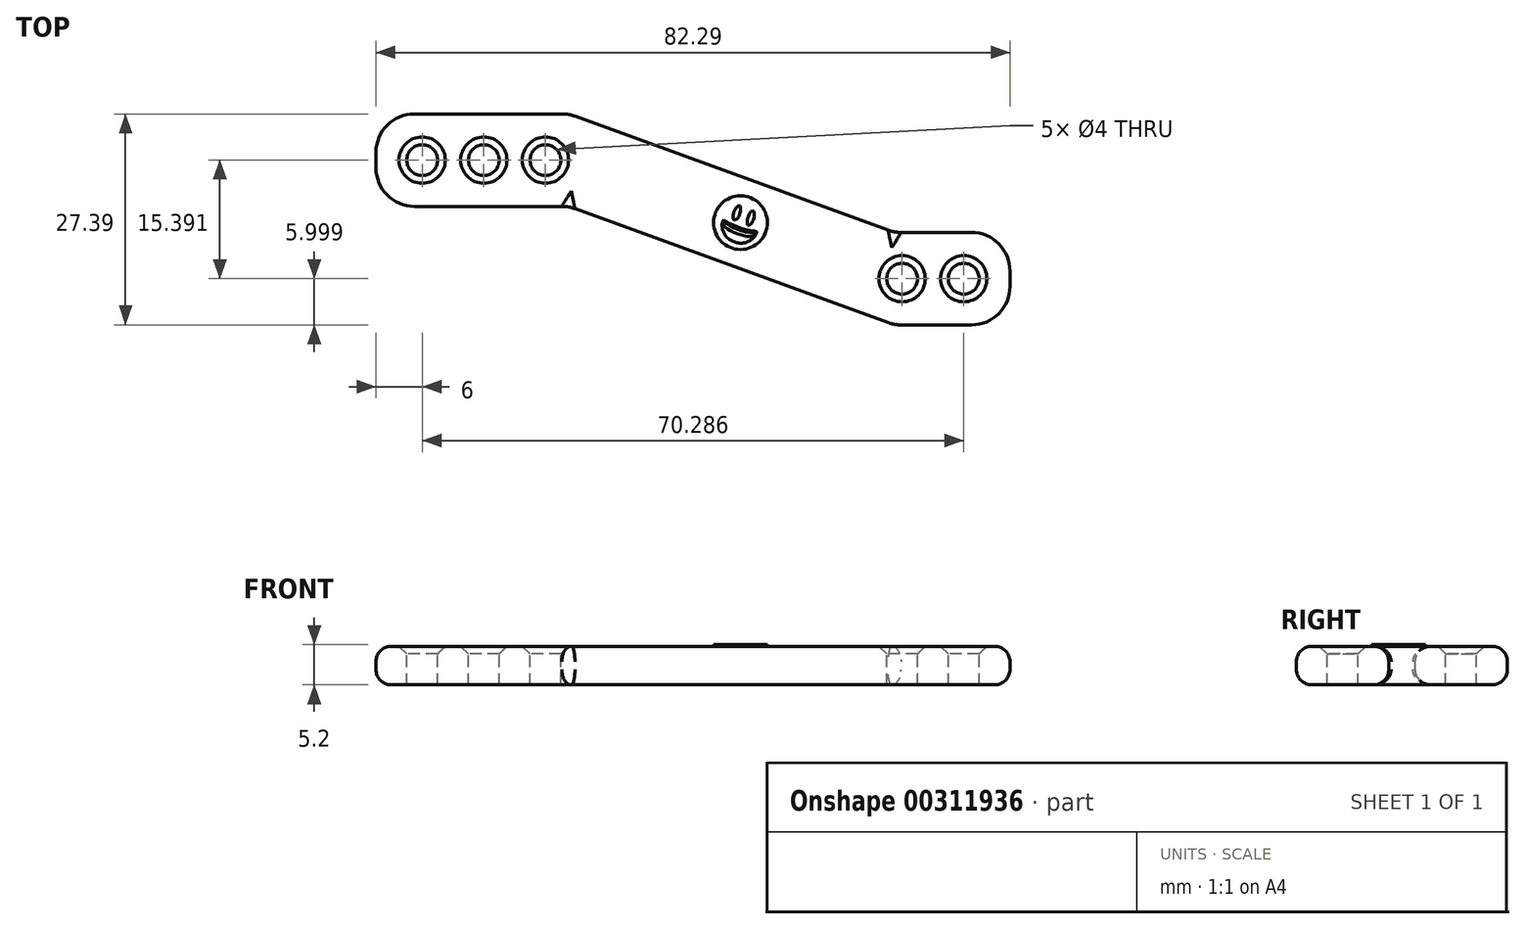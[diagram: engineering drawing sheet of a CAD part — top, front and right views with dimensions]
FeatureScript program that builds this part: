
annotation { "Feature Type Name" : "Feature", "Feature Type Description" : "" }
export const myFeature = defineFeature(function(context is Context, id is Id, definition is map)
    precondition{}
    {
        {
            var Q0;
            Q0=qCreatedBy(makeId("Top.planeOp"),FACE);
            var sketch = newSketch(context, id + "F0", { "sketchPlane" : qUnion([Q0])});
            skLineSegment(sketch, "E0.bottom", {"start": v(0, 12) * mm, "end": v(25, 12) * mm});
            skLineSegment(sketch, "E0.top", {"start": v(0, 0) * mm, "end": v(25, 0) * mm});
            skLineSegment(sketch, "E0.left", {"start": v(0, 12) * mm, "end": v(0, 0) * mm});
            skLineSegment(sketch, "E0.right", {"start": v(25, 12) * mm, "end": v(25, 0) * mm});
            skLineSegment(sketch, "E1.bottom", {"start": v(67.29, -3.4) * mm, "end": v(82.29, -3.4) * mm});
            skLineSegment(sketch, "E1.top", {"start": v(67.29, -15.4) * mm, "end": v(82.29, -15.4) * mm});
            skLineSegment(sketch, "E1.left", {"start": v(67.29, -3.4) * mm, "end": v(67.29, -15.4) * mm});
            skLineSegment(sketch, "E1.right", {"start": v(82.29, -3.4) * mm, "end": v(82.29, -15.4) * mm});
            skLineSegment(sketch, "E2", {"start": v(67.29, -3.4) * mm, "end": v(25, 12) * mm});
            skLineSegment(sketch, "E3", {"start": v(25, 0) * mm, "end": v(67.29, -15.4) * mm});
            skSolve(sketch);
        }
        {
            var Q0;
            Q0=makeQuery(id+"F0.imprint","IMPRINT",FACE,{"disambiguationData":[TD([[makeQuery(id+"F0.imprint","IMPRINT",EDGE,{"derivedFrom":sQuery(id+"F0.wireOp",EDGE,"E0.bottom")}),-1.0]])]});
            var Q1;
            Q1=makeQuery(id+"F0.imprint","IMPRINT",FACE,{"disambiguationData":[TD([[makeQuery(id+"F0.imprint","IMPRINT",EDGE,{"derivedFrom":sQuery(id+"F0.wireOp",EDGE,"E0.right")}),1.0]])]});
            var Q2;
            Q2=makeQuery(id+"F0.imprint","IMPRINT",FACE,{"disambiguationData":[TD([[makeQuery(id+"F0.imprint","IMPRINT",EDGE,{"derivedFrom":sQuery(id+"F0.wireOp",EDGE,"E1.bottom")}),-1.0]])]});
            extrude(context, id + "F1", {"entities" : qUnion([Q0, Q1, Q2]), "depth" : 5 * mm});
        }
        {
            var Q0;
            Q0=makeQuery(id+"F1.opExtrude","CAP_FACE",FACE,{"disambiguationData":[OSD([sQuery(id+"F0.wireOp",EDGE,"E0.bottom"),sQuery(id+"F0.wireOp",EDGE,"E0.top"),sQuery(id+"F0.wireOp",EDGE,"E0.left"),sQuery(id+"F0.wireOp",EDGE,"E1.bottom"),sQuery(id+"F0.wireOp",EDGE,"E1.top"),sQuery(id+"F0.wireOp",EDGE,"E1.right"),sQuery(id+"F0.wireOp",EDGE,"E2"),sQuery(id+"F0.wireOp",EDGE,"E3")])],"isStart":false});
            var sketch = newSketch(context, id + "F2", { "sketchPlane" : qUnion([Q0])});
            skCircle(sketch, "E4", {"center": v(6, 6) * mm, "radius": 2 * mm});
            skCircle(sketch, "E5", {"center": v(76.29, -9.4) * mm, "radius": 2 * mm});
            skPoint(sketch, "E5.centerSnap0", {"position": v(74.79, -3.4) * mm});
            skCircle(sketch, "E6.1.0.0", {"center": v(14, 6) * mm, "radius": 2 * mm});
            skCircle(sketch, "E6.2.0.0", {"center": v(22, 6) * mm, "radius": 2 * mm});
            skLineSegment(sketch, "E6.direction1", {"start": v(6, 6) * mm, "end": v(14, 6) * mm, "construction": true});
            skCircle(sketch, "E7.1.0.0", {"center": v(68.29, -9.4) * mm, "radius": 2 * mm});
            skLineSegment(sketch, "E7.direction1", {"start": v(76.29, -9.4) * mm, "end": v(68.29, -9.4) * mm, "construction": true});
            skSolve(sketch);
        }
        {
            var Q0;
            Q0 = qSketchRegion(id + "F2", true);
            extrude(context, id + "F3", {"entities" : qUnion([Q0]), "operationType" : NewBodyOperationType.REMOVE, "endBound" : BoundingType.THROUGH_ALL, "oppositeDirection" : true, "depth" : 25 * mm});
        }
        {
            var Q0;
            Q0=makeQuery(id+"F1.opExtrude","CAP_EDGE",EDGE,{"disambiguationData":[OSD([sQuery(id+"F0.wireOp",EDGE,"E3")])],"isStart":false});
            var Q1;
            Q1=makeQuery(id+"F1.opExtrude","CAP_EDGE",EDGE,{"disambiguationData":[OSD([sQuery(id+"F0.wireOp",EDGE,"E0.top")])],"isStart":false});
            var Q2;
            Q2=makeQuery(id+"F1.opExtrude","CAP_EDGE",EDGE,{"disambiguationData":[OSD([sQuery(id+"F0.wireOp",EDGE,"E1.top")])],"isStart":false});
            var Q3;
            Q3=makeQuery(id+"F1.opExtrude","CAP_EDGE",EDGE,{"disambiguationData":[OSD([sQuery(id+"F0.wireOp",EDGE,"E0.bottom")])],"isStart":false});
            var Q4;
            Q4=makeQuery(id+"F1.opExtrude","CAP_EDGE",EDGE,{"disambiguationData":[OSD([sQuery(id+"F0.wireOp",EDGE,"E2")])],"isStart":false});
            var Q5;
            Q5=makeQuery(id+"F1.opExtrude","CAP_EDGE",EDGE,{"disambiguationData":[OSD([sQuery(id+"F0.wireOp",EDGE,"E1.bottom")])],"isStart":false});
            var Q6;
            Q6=makeQuery(id+"F1.opExtrude","CAP_EDGE",EDGE,{"disambiguationData":[OSD([sQuery(id+"F0.wireOp",EDGE,"E0.left")])],"isStart":false});
            var Q7;
            Q7=makeQuery(id+"F1.opExtrude","CAP_EDGE",EDGE,{"disambiguationData":[OSD([sQuery(id+"F0.wireOp",EDGE,"E1.right")])],"isStart":false});
            var Q8;
            Q8=makeQuery(id+"F1.opExtrude","CAP_EDGE",EDGE,{"disambiguationData":[OSD([sQuery(id+"F0.wireOp",EDGE,"E0.top")])],"isStart":true});
            var Q9;
            Q9=makeQuery(id+"F1.opExtrude","CAP_EDGE",EDGE,{"disambiguationData":[OSD([sQuery(id+"F0.wireOp",EDGE,"E3")])],"isStart":true});
            var Q10;
            Q10=makeQuery(id+"F1.opExtrude","CAP_EDGE",EDGE,{"disambiguationData":[OSD([sQuery(id+"F0.wireOp",EDGE,"E1.top")])],"isStart":true});
            var Q11;
            Q11=makeQuery(id+"F1.opExtrude","CAP_EDGE",EDGE,{"disambiguationData":[OSD([sQuery(id+"F0.wireOp",EDGE,"E1.right")])],"isStart":true});
            var Q12;
            Q12=makeQuery(id+"F1.opExtrude","CAP_EDGE",EDGE,{"disambiguationData":[OSD([sQuery(id+"F0.wireOp",EDGE,"E1.bottom")])],"isStart":true});
            var Q13;
            Q13=makeQuery(id+"F1.opExtrude","CAP_EDGE",EDGE,{"disambiguationData":[OSD([sQuery(id+"F0.wireOp",EDGE,"E2")])],"isStart":true});
            var Q14;
            Q14=makeQuery(id+"F1.opExtrude","CAP_EDGE",EDGE,{"disambiguationData":[OSD([sQuery(id+"F0.wireOp",EDGE,"E0.bottom")])],"isStart":true});
            var Q15;
            Q15=makeQuery(id+"F1.opExtrude","CAP_EDGE",EDGE,{"disambiguationData":[OSD([sQuery(id+"F0.wireOp",EDGE,"E0.left")])],"isStart":true});
            fillet(context, id + "F4", {"entities" : qUnion([Q0, Q1, Q2, Q3, Q4, Q5, Q6, Q7, Q8, Q9, Q10, Q11, Q12, Q13, Q14, Q15]), "radius" : 2 * mm, "tangentPropagation" : true, "allowEdgeOverflow" : false});
        }
        {
            var Q0;
            Q0=makeQuery(id+"F1.opExtrude","SWEPT_EDGE",EDGE,{"disambiguationData":[OSD([sQuery(id+"F0.wireOp",EDGE,"E0.top"),sQuery(id+"F0.wireOp",EDGE,"E0.left")])]});
            var Q1;
            Q1=makeQuery(id+"F1.opExtrude","SWEPT_EDGE",EDGE,{"disambiguationData":[OSD([sQuery(id+"F0.wireOp",EDGE,"E0.top"),sQuery(id+"F0.wireOp",EDGE,"E0.right"),sQuery(id+"F0.wireOp",EDGE,"E3")])]});
            var Q2;
            Q2=makeQuery(id+"F1.opExtrude","SWEPT_EDGE",EDGE,{"disambiguationData":[OSD([sQuery(id+"F0.wireOp",EDGE,"E1.top"),sQuery(id+"F0.wireOp",EDGE,"E1.left"),sQuery(id+"F0.wireOp",EDGE,"E3")])]});
            var Q3;
            Q3=makeQuery(id+"F1.opExtrude","SWEPT_EDGE",EDGE,{"disambiguationData":[OSD([sQuery(id+"F0.wireOp",EDGE,"E1.top"),sQuery(id+"F0.wireOp",EDGE,"E1.right")])]});
            var Q4;
            Q4=makeQuery(id+"F1.opExtrude","SWEPT_EDGE",EDGE,{"disambiguationData":[OSD([sQuery(id+"F0.wireOp",EDGE,"E1.bottom"),sQuery(id+"F0.wireOp",EDGE,"E1.right")])]});
            var Q5;
            Q5=makeQuery(id+"F1.opExtrude","SWEPT_EDGE",EDGE,{"disambiguationData":[OSD([sQuery(id+"F0.wireOp",EDGE,"E1.bottom"),sQuery(id+"F0.wireOp",EDGE,"E1.left"),sQuery(id+"F0.wireOp",EDGE,"E2")])]});
            var Q6;
            Q6=makeQuery(id+"F1.opExtrude","SWEPT_EDGE",EDGE,{"disambiguationData":[OSD([sQuery(id+"F0.wireOp",EDGE,"E0.bottom"),sQuery(id+"F0.wireOp",EDGE,"E0.right"),sQuery(id+"F0.wireOp",EDGE,"E2")])]});
            var Q7;
            Q7=makeQuery(id+"F1.opExtrude","SWEPT_EDGE",EDGE,{"disambiguationData":[OSD([sQuery(id+"F0.wireOp",EDGE,"E0.bottom"),sQuery(id+"F0.wireOp",EDGE,"E0.left")])]});
            fillet(context, id + "F5", {"entities" : qUnion([Q0, Q1, Q2, Q3, Q4, Q5, Q6, Q7]), "radius" : 5 * mm, "tangentPropagation" : true, "allowEdgeOverflow" : false});
        }
        {
            var Q0;
            Q0=makeQuery(id+"F1.opExtrude","CAP_FACE",FACE,{"disambiguationData":[OSD([sQuery(id+"F0.wireOp",EDGE,"E0.bottom"),sQuery(id+"F0.wireOp",EDGE,"E0.top"),sQuery(id+"F0.wireOp",EDGE,"E0.left"),sQuery(id+"F0.wireOp",EDGE,"E1.bottom"),sQuery(id+"F0.wireOp",EDGE,"E1.top"),sQuery(id+"F0.wireOp",EDGE,"E1.right"),sQuery(id+"F0.wireOp",EDGE,"E2"),sQuery(id+"F0.wireOp",EDGE,"E3")])],"isStart":false});
            chamfer(context, id + "F6", {"entities" : qUnion([Q0]), "width" : 1 * mm, "tangentPropagation" : true});
        }
        {
            var Q0;
            Q0=makeQuery(id+"F1.opExtrude","CAP_FACE",FACE,{"disambiguationData":[OSD([sQuery(id+"F0.wireOp",EDGE,"E0.bottom"),sQuery(id+"F0.wireOp",EDGE,"E0.top"),sQuery(id+"F0.wireOp",EDGE,"E0.left"),sQuery(id+"F0.wireOp",EDGE,"E1.bottom"),sQuery(id+"F0.wireOp",EDGE,"E1.top"),sQuery(id+"F0.wireOp",EDGE,"E1.right"),sQuery(id+"F0.wireOp",EDGE,"E2"),sQuery(id+"F0.wireOp",EDGE,"E3")])],"isStart":false});
            var sketch = newSketch(context, id + "F7", { "sketchPlane" : qUnion([Q0])});
            skPoint(sketch, "E8.firstSnap0", {"position": v(2.88, 2.88) * mm});
            skPoint(sketch, "E9", {"position": v(46.25, -5.6) * mm});
            skCircle(sketch, "E10", {"center": v(47.3, -2.12) * mm, "radius": 3.49 * mm});
            skFitSpline(sketch, "E11", {"points": [v(46.43, -0.77) * mm, v(46.67, -0.3) * mm, v(46.8, -0.12) * mm, v(46.96, 0) * mm, v(47.11, 0.08) * mm, v(47.26, 0) * mm, v(47.32, -0.33) * mm, v(47.29, -0.67) * mm, v(47.16, -1.14) * mm, v(46.93, -1.53) * mm, v(46.78, -1.66) * mm, v(46.57, -1.78) * mm, v(46.38, -1.66) * mm, v(46.35, -1.38) * mm, v(46.38, -1.03) * mm, v(46.43, -0.77) * mm]});
            skFitSpline(sketch, "E12", {"points": [v(48.31, -1.37) * mm, v(48.44, -1.06) * mm, v(48.63, -0.77) * mm, v(48.85, -0.61) * mm, v(49.04, -0.65) * mm, v(49.1, -0.87) * mm, v(49.11, -1.22) * mm, v(49.04, -1.55) * mm, v(48.9, -1.94) * mm, v(48.72, -2.22) * mm, v(48.51, -2.4) * mm, v(48.28, -2.42) * mm, v(48.18, -2.24) * mm, v(48.17, -1.94) * mm, v(48.22, -1.58) * mm, v(48.31, -1.37) * mm]});
            skFitSpline(sketch, "E13", {"points": [v(45.17, -1.76) * mm, v(45.47, -1.97) * mm, v(46.03, -2.28) * mm, v(46.76, -2.6) * mm, v(47.22, -2.8) * mm, v(48.28, -3.1) * mm, v(49.12, -3.2) * mm, v(49.37, -3.26) * mm, v(49.24, -3.76) * mm, v(48.74, -4.3) * mm, v(48.08, -4.66) * mm, v(47.33, -4.78) * mm, v(46.55, -4.64) * mm, v(45.86, -4.27) * mm, v(45.24, -3.64) * mm, v(44.98, -2.97) * mm, v(44.9, -2.36) * mm, v(45.03, -1.9) * mm, v(45.17, -1.76) * mm]});
            skFitSpline(sketch, "E14", {"points": [v(45.24, -2.15) * mm, v(46.02, -2.58) * mm, v(47.08, -3.04) * mm, v(48.27, -3.38) * mm, v(49, -3.53) * mm, v(48.89, -3.85) * mm, v(48.1, -3.87) * mm, v(46.92, -3.58) * mm, v(45.88, -3.1) * mm, v(45.32, -2.74) * mm, v(45.15, -2.51) * mm, v(45.24, -2.15) * mm]});
            skSolve(sketch);
        }
        {
            var Q0;
            Q0=makeQuery(id+"F7.imprint","IMPRINT",FACE,{"disambiguationData":[TD([[makeQuery(id+"F7.imprint","IMPRINT",EDGE,{"derivedFrom":sQuery(id+"F7.wireOp",EDGE,"E14")}),-1.0]])]});
            var Q1;
            Q1=makeQuery(id+"F7.imprint","IMPRINT",FACE,{"disambiguationData":[TD([[makeQuery(id+"F7.imprint","IMPRINT",EDGE,{"derivedFrom":sQuery(id+"F7.wireOp",EDGE,"E10")}),1.0]])]});
            extrude(context, id + "F8", {"entities" : qUnion([Q0, Q1]), "operationType" : NewBodyOperationType.ADD, "depth" : 0.2 * mm});
        }
    });
